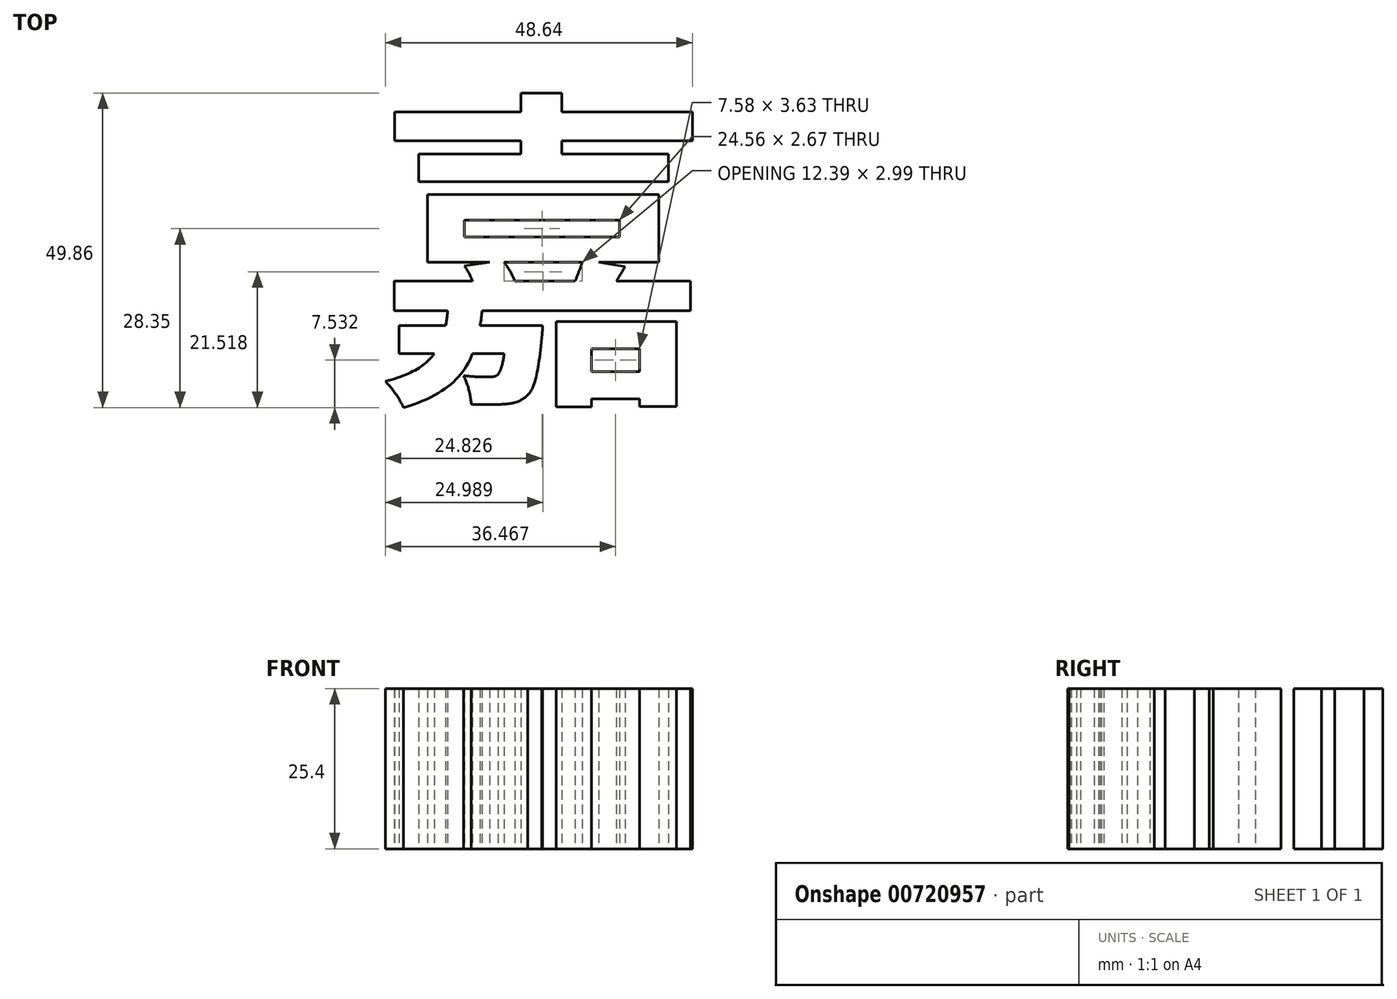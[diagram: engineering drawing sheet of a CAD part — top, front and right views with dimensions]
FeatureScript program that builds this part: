
annotation { "Feature Type Name" : "Feature", "Feature Type Description" : "" }
export const myFeature = defineFeature(function(context is Context, id is Id, definition is map)
    precondition{}
    {
        {
            var Q0;
            Q0=qCreatedBy(makeId("Top.planeOp"),FACE);
            var sketch = newSketch(context, id + "F0", { "sketchPlane" : qUnion([Q0])});
            skText(sketch, "E0", { "text": "嘉", "fontName": "NotoSansCJKtc-Bold.otf"});
            const initialGuessF0  = {"E0": [-0.02817, -0.0199, 1, 0, 0.03844]};
            skSetInitialGuess(sketch, initialGuessF0);
            skSolve(sketch);
        }
        {
            var Q0;
            Q0 = qSketchRegion(id + "F0", true);
            extrude(context, id + "F1", {"entities" : qUnion([Q0]), "depth" : 25.4 * mm, "offsetDistance" : 25.4 * mm});
        }
    });
